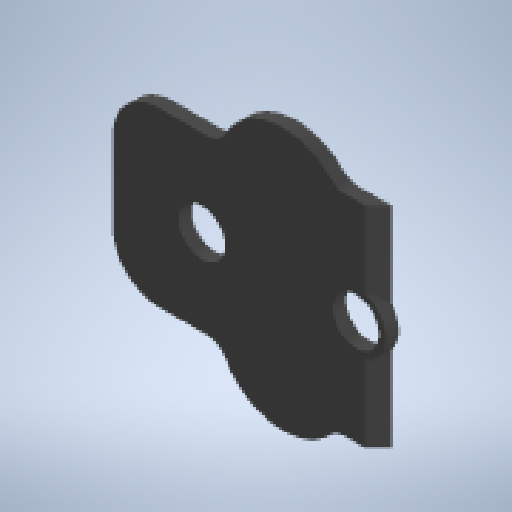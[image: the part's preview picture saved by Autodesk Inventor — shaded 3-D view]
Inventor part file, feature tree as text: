
AUTODESK INVENTOR PART (.ipt)
format: ipt  version: 2025.2 (Build 292293000, 293)  size: 171,520 bytes
history: native  units: mm
features: other x1, extrude x1, mirror x1, sketch x1
ambient origin geometry x8: Origin, YZ Plane, XZ Plane, XY Plane, X Axis, Y Axis, Z Axis, Center Point
bodies: Body1 (feature_tree)
feature tree (4):
  other  "Sólido1"
  extrude  "Extrusão1"  Depth=2.0mm
  mirror  "Espelhar1"
  sketch  "Esboço1"  dims[d2=2.0mm d3=0.0mm d4=5.0mm d5=5.0mm d6=25.0mm d7=13.4mm d10=40.0mm d11=40.0mm d12=13.6mm d14=20.0mm d15=14.72mm d16=11.0mm d17=20.0mm d18=3.0mm d19=13.0mm d20=7.0mm d21=15.81mm d29=2.0mm]
